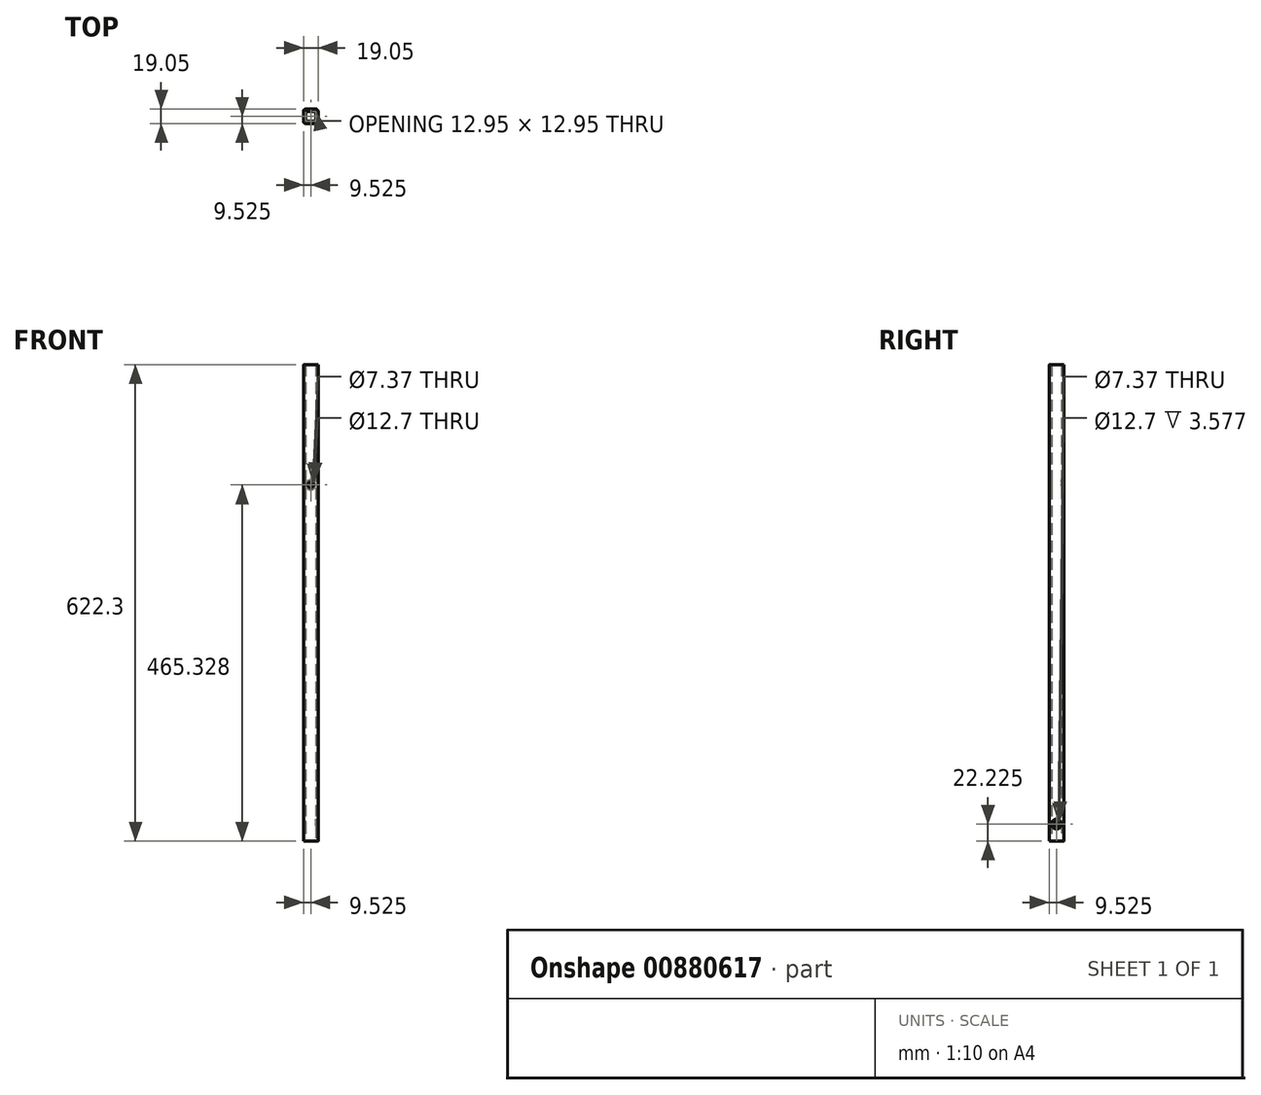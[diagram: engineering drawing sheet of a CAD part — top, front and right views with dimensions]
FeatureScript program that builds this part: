
annotation { "Feature Type Name" : "Feature", "Feature Type Description" : "" }
export const myFeature = defineFeature(function(context is Context, id is Id, definition is map)
    precondition{}
    {
        {
            var Q0;
            Q0=qCreatedBy(makeId("Top.planeOp"),FACE);
            var sketch = newSketch(context, id + "F0", { "sketchPlane" : qUnion([Q0])});
            skLineSegment(sketch, "E0.bottom", {"start": v(3.18, 0) * mm, "end": v(15.87, 0) * mm});
            skLineSegment(sketch, "E0.top", {"start": v(3.18, 19.05) * mm, "end": v(15.88, 19.05) * mm});
            skLineSegment(sketch, "E0.left", {"start": v(0, 3.18) * mm, "end": v(0, 15.87) * mm});
            skLineSegment(sketch, "E0.right", {"start": v(19.05, 3.18) * mm, "end": v(19.05, 15.87) * mm});
            skLineSegment(sketch, "E1.0", {"start": v(4.06, 16) * mm, "end": v(14.99, 16) * mm});
            skLineSegment(sketch, "E1.1", {"start": v(3.05, 4.06) * mm, "end": v(3.05, 14.99) * mm});
            skLineSegment(sketch, "E1.2", {"start": v(4.06, 3.05) * mm, "end": v(14.99, 3.05) * mm});
            skLineSegment(sketch, "E1.3", {"start": v(16, 4.06) * mm, "end": v(16, 14.99) * mm});
            skPoint(sketch, "E2.visualSharp", {"position": v(19.05, 19.05) * mm});
            skArc(sketch, "E2.filletArc", {"start": v(19.05, 15.88) * mm, "mid": v(18.12, 18.12) * mm, "end": v(15.88, 19.05) * mm});
            skPoint(sketch, "E3.visualSharp", {"position": v(19.05, 0) * mm});
            skArc(sketch, "E3.filletArc", {"start": v(15.87, 0) * mm, "mid": v(18.12, 0.93) * mm, "end": v(19.05, 3.18) * mm});
            skPoint(sketch, "E4.visualSharp", {"position": v(0, 0) * mm});
            skArc(sketch, "E4.filletArc", {"start": v(0, 3.17) * mm, "mid": v(0.93, 0.93) * mm, "end": v(3.18, 0) * mm});
            skPoint(sketch, "E5.visualSharp", {"position": v(0, 19.05) * mm});
            skArc(sketch, "E5.filletArc", {"start": v(3.18, 19.05) * mm, "mid": v(0.93, 18.12) * mm, "end": v(0, 15.88) * mm});
            skPoint(sketch, "E6.visualSharp", {"position": v(3.05, 16) * mm});
            skArc(sketch, "E6.filletArc", {"start": v(4.06, 16) * mm, "mid": v(3.35, 15.7) * mm, "end": v(3.05, 14.99) * mm});
            skPoint(sketch, "E7.visualSharp", {"position": v(16, 3.05) * mm});
            skArc(sketch, "E7.filletArc", {"start": v(14.99, 3.05) * mm, "mid": v(15.7, 3.35) * mm, "end": v(16, 4.06) * mm});
            skPoint(sketch, "E8.visualSharp", {"position": v(3.05, 3.05) * mm});
            skArc(sketch, "E8.filletArc", {"start": v(3.05, 4.06) * mm, "mid": v(3.35, 3.35) * mm, "end": v(4.06, 3.05) * mm});
            skPoint(sketch, "E9.visualSharp", {"position": v(16, 16) * mm});
            skArc(sketch, "E9.filletArc", {"start": v(16, 14.99) * mm, "mid": v(15.7, 15.7) * mm, "end": v(14.99, 16) * mm});
            skSolve(sketch);
        }
        {
            var Q0;
            Q0 = qSketchRegion(id + "F0", true);
            extrude(context, id + "F1", {"entities" : qUnion([Q0]), "depth" : 622.3 * mm, "offsetDistance" : 25.4 * mm});
        }
        {
            var Q0;
            Q0=qCreatedBy(makeId("Right.planeOp"),FACE);
            var sketch = newSketch(context, id + "F2", { "sketchPlane" : qUnion([Q0])});
            skCircle(sketch, "E10", {"center": v(9.53, 22.23) * mm, "radius": 3.68 * mm});
            skLineSegment(sketch, "E11", {"start": v(0, 22.23) * mm, "end": v(19.05, 22.23) * mm, "construction": true});
            skSolve(sketch);
        }
        {
            var Q0;
            Q0=makeQuery(id+"F2.imprint","IMPRINT",FACE,{"disambiguationData":[TD([[makeQuery(id+"F2.imprint","IMPRINT",EDGE,{"derivedFrom":sQuery(id+"F2.wireOp",EDGE,"E10")}),1.0]])]});
            var Q1;
            Q1=sQuery(id+"F2.wireOp",EDGE,"E10");
            extrude(context, id + "F3", {"entities" : qUnion([Q0]), "operationType" : NewBodyOperationType.REMOVE, "surfaceEntities" : qUnion([Q1]), "depth" : 47.5 * mm, "offsetDistance" : 25.4 * mm});
        }
        {
            var Q0;
            Q0=makeQuery(id+"F1.opExtrude","SWEPT_FACE",FACE,{"disambiguationData":[OSD([sQuery(id+"F0.wireOp",EDGE,"E0.right")])]});
            var sketch = newSketch(context, id + "F4", { "sketchPlane" : qUnion([Q0])});
            skCircle(sketch, "E12", {"center": v(9.53, 22.23) * mm, "radius": 6.35 * mm});
            skSolve(sketch);
        }
        {
            var Q0;
            Q0 = qSketchRegion(id + "F4", true);
            extrude(context, id + "F5", {"entities" : qUnion([Q0]), "operationType" : NewBodyOperationType.REMOVE, "oppositeDirection" : true, "depth" : 4.06 * mm, "offsetDistance" : 25.4 * mm});
        }
        {
            var Q0;
            Q0=qCreatedBy(makeId("Front.planeOp"),FACE);
            var sketch = newSketch(context, id + "F6", { "sketchPlane" : qUnion([Q0])});
            skCircle(sketch, "E13", {"center": v(9.53, 465.33) * mm, "radius": 3.68 * mm});
            skLineSegment(sketch, "E14", {"start": v(9.53, 465.33) * mm, "end": v(0, 465.33) * mm, "construction": true});
            skLineSegment(sketch, "E15", {"start": v(9.53, 465.33) * mm, "end": v(19.05, 465.33) * mm, "construction": true});
            skSolve(sketch);
        }
        {
            var Q0;
            Q0 = qSketchRegion(id + "F6", true);
            extrude(context, id + "F7", {"entities" : qUnion([Q0]), "operationType" : NewBodyOperationType.REMOVE, "oppositeDirection" : true, "depth" : 25.4 * mm, "offsetDistance" : 25.4 * mm});
        }
        {
            var Q0;
            Q0=makeQuery(id+"F1.opExtrude","SWEPT_FACE",FACE,{"disambiguationData":[OSD([sQuery(id+"F0.wireOp",EDGE,"E0.top")])]});
            var sketch = newSketch(context, id + "F8", { "sketchPlane" : qUnion([Q0])});
            skCircle(sketch, "E16", {"center": v(-9.53, 465.33) * mm, "radius": 6.35 * mm});
            skSolve(sketch);
        }
        {
            var Q0;
            Q0 = qSketchRegion(id + "F8", true);
            extrude(context, id + "F9", {"entities" : qUnion([Q0]), "operationType" : NewBodyOperationType.REMOVE, "oppositeDirection" : true, "depth" : 8.64 * mm, "offsetDistance" : 25.4 * mm});
        }
    });
